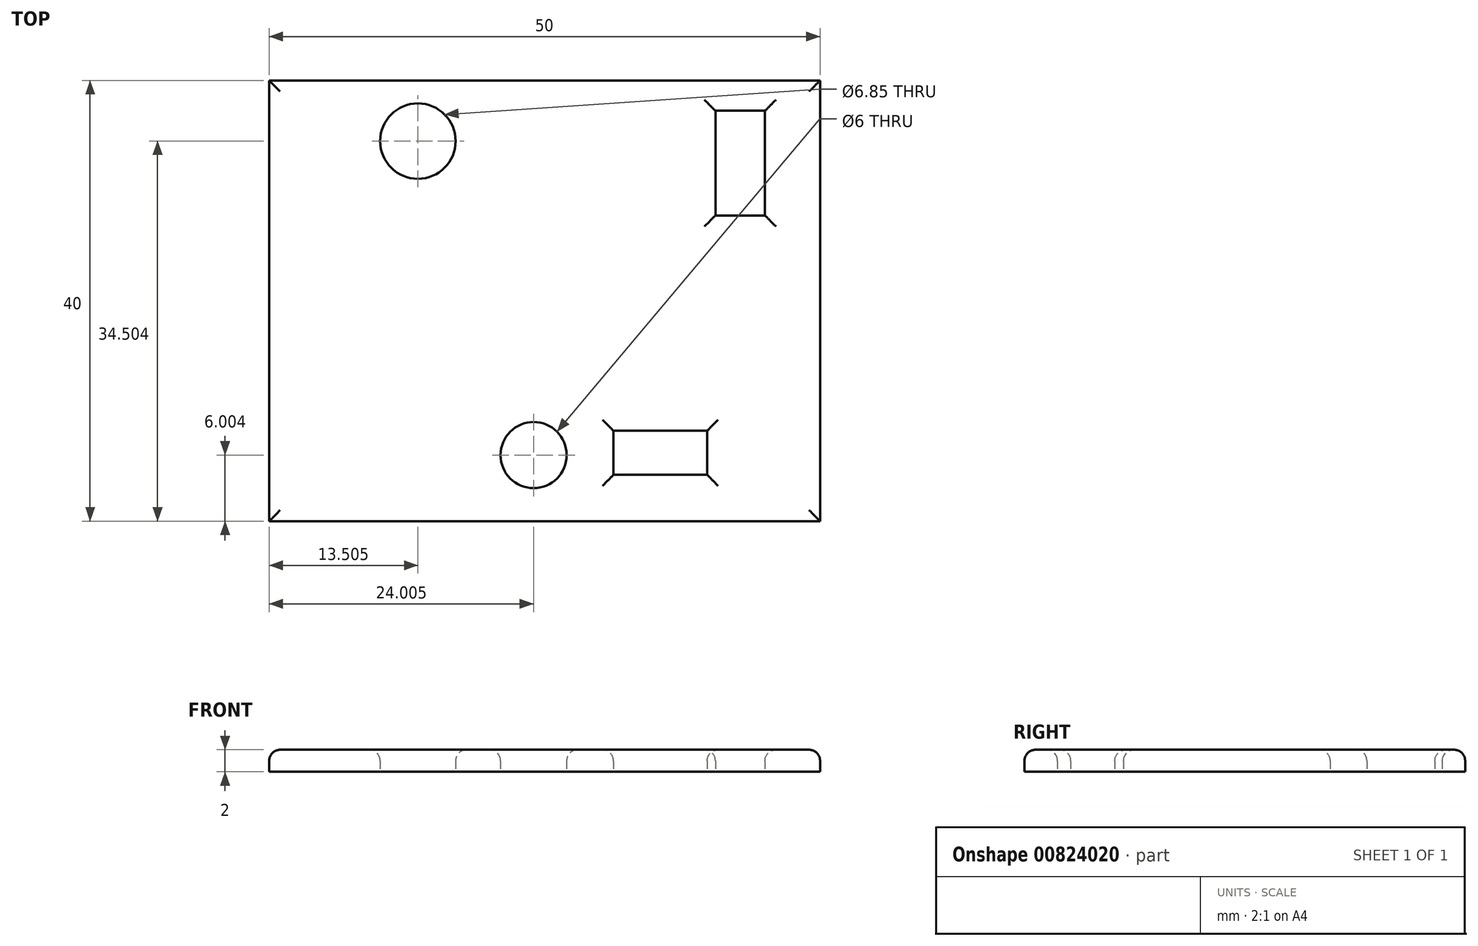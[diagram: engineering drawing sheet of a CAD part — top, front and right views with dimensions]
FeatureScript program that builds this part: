
annotation { "Feature Type Name" : "Feature", "Feature Type Description" : "" }
export const myFeature = defineFeature(function(context is Context, id is Id, definition is map)
    precondition{}
    {
        {
            var Q0;
            Q0=qCreatedBy(makeId("Top.planeOp"),FACE);
            var sketch = newSketch(context, id + "F0", { "sketchPlane" : qUnion([Q0])});
            skLineSegment(sketch, "E0.bottom", {"start": v(-13.97, 35.01) * mm, "end": v(36.03, 35.01) * mm});
            skLineSegment(sketch, "E0.top", {"start": v(-13.97, -4.99) * mm, "end": v(36.03, -4.99) * mm});
            skLineSegment(sketch, "E0.left", {"start": v(-13.97, 35.01) * mm, "end": v(-13.97, -4.99) * mm});
            skLineSegment(sketch, "E0.right", {"start": v(36.03, 35.01) * mm, "end": v(36.03, -4.99) * mm});
            skCircle(sketch, "E1", {"center": v(-0.47, 29.51) * mm, "radius": 3.43 * mm});
            skLineSegment(sketch, "E2.bottom", {"start": v(26.53, 32.26) * mm, "end": v(31.03, 32.26) * mm});
            skLineSegment(sketch, "E2.top", {"start": v(26.53, 22.76) * mm, "end": v(31.03, 22.76) * mm});
            skLineSegment(sketch, "E2.left", {"start": v(26.53, 32.26) * mm, "end": v(26.53, 22.76) * mm});
            skLineSegment(sketch, "E2.right", {"start": v(31.03, 32.26) * mm, "end": v(31.03, 22.76) * mm});
            skCircle(sketch, "E3", {"center": v(10.03, 1.01) * mm, "radius": 3 * mm});
            skLineSegment(sketch, "E4.bottom", {"start": v(17.28, 3.21) * mm, "end": v(25.78, 3.21) * mm});
            skLineSegment(sketch, "E4.top", {"start": v(17.28, -0.79) * mm, "end": v(25.78, -0.79) * mm});
            skLineSegment(sketch, "E4.left", {"start": v(17.28, 3.21) * mm, "end": v(17.28, -0.79) * mm});
            skLineSegment(sketch, "E4.right", {"start": v(25.78, 3.21) * mm, "end": v(25.78, -0.79) * mm});
            skSolve(sketch);
        }
        {
            var Q0;
            Q0=makeQuery(id+"F0.imprint","IMPRINT",FACE,{"disambiguationData":[TD([[makeQuery(id+"F0.imprint","IMPRINT",EDGE,{"derivedFrom":sQuery(id+"F0.wireOp",EDGE,"E0.bottom")}),-1.0]])]});
            extrude(context, id + "F1", {"entities" : qUnion([Q0]), "depth" : 2 * mm, "offsetDistance" : 25 * mm});
        }
        {
            var Q0;
            Q0=makeQuery(id+"F1.opExtrude","CAP_EDGE",EDGE,{"disambiguationData":[OSD([sQuery(id+"F0.wireOp",EDGE,"E2.right")])],"isStart":false});
            var Q1;
            Q1=makeQuery(id+"F1.opExtrude","CAP_EDGE",EDGE,{"disambiguationData":[OSD([sQuery(id+"F0.wireOp",EDGE,"E2.top")])],"isStart":false});
            var Q2;
            Q2=makeQuery(id+"F1.opExtrude","CAP_EDGE",EDGE,{"disambiguationData":[OSD([sQuery(id+"F0.wireOp",EDGE,"E2.left")])],"isStart":false});
            var Q3;
            Q3=makeQuery(id+"F1.opExtrude","CAP_EDGE",EDGE,{"disambiguationData":[OSD([sQuery(id+"F0.wireOp",EDGE,"E2.bottom")])],"isStart":false});
            var Q4;
            Q4=makeQuery(id+"F1.opExtrude","CAP_EDGE",EDGE,{"disambiguationData":[OSD([sQuery(id+"F0.wireOp",EDGE,"E4.left")])],"isStart":false});
            var Q5;
            Q5=makeQuery(id+"F1.opExtrude","CAP_EDGE",EDGE,{"disambiguationData":[OSD([sQuery(id+"F0.wireOp",EDGE,"E4.top")])],"isStart":false});
            var Q6;
            Q6=makeQuery(id+"F1.opExtrude","CAP_EDGE",EDGE,{"disambiguationData":[OSD([sQuery(id+"F0.wireOp",EDGE,"E4.right")])],"isStart":false});
            var Q7;
            Q7=makeQuery(id+"F1.opExtrude","CAP_EDGE",EDGE,{"disambiguationData":[OSD([sQuery(id+"F0.wireOp",EDGE,"E4.bottom")])],"isStart":false});
            var Q8;
            Q8=makeQuery(id+"F1.opExtrude","CAP_EDGE",EDGE,{"disambiguationData":[OSD([sQuery(id+"F0.wireOp",EDGE,"E3")])],"isStart":false});
            var Q9;
            Q9=makeQuery(id+"F1.opExtrude","CAP_EDGE",EDGE,{"disambiguationData":[OSD([sQuery(id+"F0.wireOp",EDGE,"E1")])],"isStart":false});
            var Q10;
            Q10=makeQuery(id+"F1.opExtrude","CAP_EDGE",EDGE,{"disambiguationData":[OSD([sQuery(id+"F0.wireOp",EDGE,"E0.bottom")])],"isStart":false});
            var Q11;
            Q11=makeQuery(id+"F1.opExtrude","CAP_EDGE",EDGE,{"disambiguationData":[OSD([sQuery(id+"F0.wireOp",EDGE,"E0.left")])],"isStart":false});
            var Q12;
            Q12=makeQuery(id+"F1.opExtrude","CAP_EDGE",EDGE,{"disambiguationData":[OSD([sQuery(id+"F0.wireOp",EDGE,"E0.right")])],"isStart":false});
            var Q13;
            Q13=makeQuery(id+"F1.opExtrude","CAP_EDGE",EDGE,{"disambiguationData":[OSD([sQuery(id+"F0.wireOp",EDGE,"E0.top")])],"isStart":false});
            fillet(context, id + "F2", {"entities" : qUnion([Q0, Q1, Q2, Q3, Q4, Q5, Q6, Q7, Q8, Q9, Q10, Q11, Q12, Q13]), "radius" : 1 * mm, "tangentPropagation" : true, "allowEdgeOverflow" : false});
        }
    });
